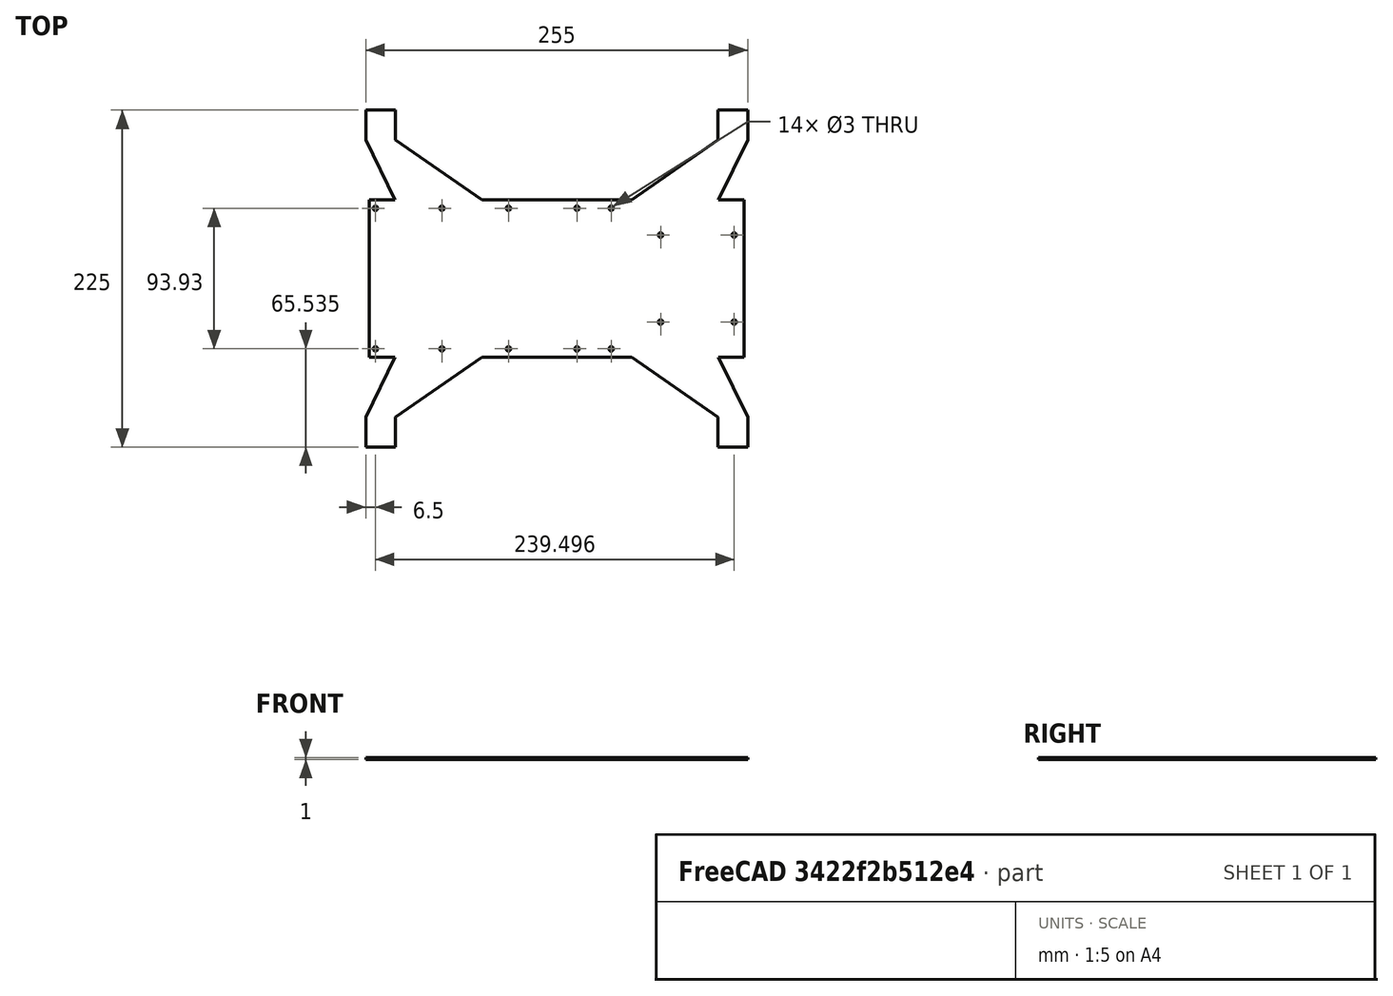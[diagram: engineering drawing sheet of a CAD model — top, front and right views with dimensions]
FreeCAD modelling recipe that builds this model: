
FCSTD DOCUMENT  (FreeCAD 0.20R25742 (Git))
Label: Electronics_Standoff
License: All rights reserved
LicenseURL: http://en.wikipedia.org/wiki/All_rights_reserved
objects: TechDraw::DrawViewDimension×2, Sketcher::SketchObject×1, PartDesign::Pad×1, PartDesign::Body×1, TechDraw::DrawSVGTemplate×1, TechDraw::DrawProjGroupItem×1, TechDraw::DrawProjGroup×1, TechDraw::DrawPage×1
note: 4 computed .brp shape members not serialized (recipe doc carries the construction recipe); baked Part::Feature solids carry a one-line shape summary decoded from their .brp

FEATURE [Sketcher::SketchObject] Sketch
  FullyConstrained = true
  MapMode = 5
  Support = -> [XY_Plane]
  sketch-geometry (42):
    g0: LineSegment StartX=-125 StartY=52.5 StartZ=0 EndX=-108 EndY=52.5 EndZ=0
    g1: LineSegment StartX=125 StartY=52.5 StartZ=0 EndX=125 EndY=-52.5 EndZ=0
    g2: LineSegment StartX=125 StartY=-52.5 StartZ=0 EndX=108 EndY=-52.5 EndZ=0
    g3: LineSegment StartX=-125 StartY=-52.5 StartZ=0 EndX=-125 EndY=52.5 EndZ=0
    g4: Circle CenterX=-121 CenterY=-46.965 CenterZ=0 NormalX=0 NormalY=0 NormalZ=1 AngleXU=0 Radius=1.5
    g5: Circle CenterX=-76.58 CenterY=-46.965 CenterZ=0 NormalX=0 NormalY=0 NormalZ=1 AngleXU=0 Radius=1.5
    g6: Circle CenterX=-32.16 CenterY=-46.965 CenterZ=0 NormalX=0 NormalY=0 NormalZ=1 AngleXU=0 Radius=1.5
    g7: Circle CenterX=13.54 CenterY=-46.965 CenterZ=0 NormalX=0 NormalY=0 NormalZ=1 AngleXU=0 Radius=1.5
    g8: Circle CenterX=36.41 CenterY=-46.965 CenterZ=0 NormalX=0 NormalY=0 NormalZ=1 AngleXU=0 Radius=1.5
    g9: Circle CenterX=36.41 CenterY=46.965 CenterZ=0 NormalX=0 NormalY=0 NormalZ=1 AngleXU=0 Radius=1.5
    g10: Circle CenterX=13.54 CenterY=46.965 CenterZ=0 NormalX=0 NormalY=0 NormalZ=1 AngleXU=0 Radius=1.5
    g11: Circle CenterX=-32.16 CenterY=46.965 CenterZ=0 NormalX=0 NormalY=0 NormalZ=1 AngleXU=0 Radius=1.5
    g12: Circle CenterX=-76.58 CenterY=46.965 CenterZ=0 NormalX=0 NormalY=0 NormalZ=1 AngleXU=0 Radius=1.5
    g13: Circle CenterX=-121 CenterY=46.965 CenterZ=0 NormalX=0 NormalY=0 NormalZ=1 AngleXU=0 Radius=1.5
    g14: Circle CenterX=69.3563 CenterY=29.07 CenterZ=0 NormalX=0 NormalY=0 NormalZ=1 AngleXU=0 Radius=1.5
    g15: Circle CenterX=118.496 CenterY=29.07 CenterZ=0 NormalX=0 NormalY=0 NormalZ=1 AngleXU=0 Radius=1.5
    g16: Circle CenterX=69.3563 CenterY=-29.07 CenterZ=0 NormalX=0 NormalY=0 NormalZ=1 AngleXU=0 Radius=1.5
    g17: Circle CenterX=118.496 CenterY=-29.07 CenterZ=0 NormalX=0 NormalY=0 NormalZ=1 AngleXU=0 Radius=1.5
    g18: LineSegment StartX=108 StartY=52.5 StartZ=0 EndX=127.5 EndY=92.5 EndZ=0
    g19: LineSegment StartX=127.5 StartY=92.5 StartZ=0 EndX=127.5 EndY=112.5 EndZ=0
    g20: LineSegment StartX=127.5 StartY=112.5 StartZ=0 EndX=107.5 EndY=112.5 EndZ=0
    g21: LineSegment StartX=107.5 StartY=112.5 StartZ=0 EndX=107.5 EndY=92.5 EndZ=0
    g22: LineSegment StartX=107.5 StartY=92.5 StartZ=0 EndX=50 EndY=52.5 EndZ=0
    g23: LineSegment StartX=-108 StartY=52.5 StartZ=0 EndX=-127.5 EndY=92.5 EndZ=0
    g24: LineSegment StartX=-127.5 StartY=92.5 StartZ=0 EndX=-127.5 EndY=112.5 EndZ=0
    g25: LineSegment StartX=-127.5 StartY=112.5 StartZ=0 EndX=-107.5 EndY=112.5 EndZ=0
    g26: LineSegment StartX=-107.5 StartY=112.5 StartZ=0 EndX=-107.5 EndY=92.5 EndZ=0
    g27: LineSegment StartX=-107.5 StartY=92.5 StartZ=0 EndX=-50 EndY=52.5 EndZ=0
    g28: LineSegment StartX=-108 StartY=-52.5 StartZ=0 EndX=-127.5 EndY=-92.5 EndZ=0
    g29: LineSegment StartX=-127.5 StartY=-92.5 StartZ=0 EndX=-127.5 EndY=-112.5 EndZ=0
    g30: LineSegment StartX=-127.5 StartY=-112.5 StartZ=0 EndX=-107.5 EndY=-112.5 EndZ=0
    g31: LineSegment StartX=-107.5 StartY=-112.5 StartZ=0 EndX=-107.5 EndY=-92.5 EndZ=0
    g32: LineSegment StartX=-107.5 StartY=-92.5 StartZ=0 EndX=-50 EndY=-52.5 EndZ=0
    g33: LineSegment StartX=108 StartY=-52.5 StartZ=0 EndX=127.5 EndY=-92.5 EndZ=0
    g34: LineSegment StartX=127.5 StartY=-92.5 StartZ=0 EndX=127.5 EndY=-112.5 EndZ=0
    g35: LineSegment StartX=127.5 StartY=-112.5 StartZ=0 EndX=107.5 EndY=-112.5 EndZ=0
    g36: LineSegment StartX=107.5 StartY=-112.5 StartZ=0 EndX=107.5 EndY=-92.5 EndZ=0
    g37: LineSegment StartX=107.5 StartY=-92.5 StartZ=0 EndX=50 EndY=-52.5 EndZ=0
    g38: LineSegment StartX=-50 StartY=52.5 StartZ=0 EndX=50 EndY=52.5 EndZ=0
    g39: LineSegment StartX=108 StartY=52.5 StartZ=0 EndX=125 EndY=52.5 EndZ=0
    g40: LineSegment StartX=50 StartY=-52.5 StartZ=0 EndX=-50 EndY=-52.5 EndZ=0
    g41: LineSegment StartX=-108 StartY=-52.5 StartZ=0 EndX=-125 EndY=-52.5 EndZ=0
  constraints (121):
    c: Coincident(g39,g1)
    c: Coincident(g1,g2)
    c: Coincident(g41,g3)
    c: Coincident(g3,g0)
    c: Horizontal(g0)
    c: Horizontal(g2)
    c: Vertical(g1)
    c: Vertical(g3)
    c: Symmetric(g1,g0,g-1)
    c: DistanceY(g3,g3) = 105
    c: DistanceX(g0,g39) = 250
    c: Diameter(g4) = 3
    c: Horizontal(g7,g6)
    c: Horizontal(g6,g5)
    c: Horizontal(g5,g4)
    c: Horizontal(g4,g8)
    c: Horizontal(g13,g12)
    c: Horizontal(g12,g11)
    c: Horizontal(g11,g10)
    c: Horizontal(g10,g9)
    c: Equal(g4,g5)
    c: Equal(g5,g6)
    c: Equal(g6,g7)
    c: Equal(g7,g8)
    c: Equal(g8,g9)
    c: Equal(g9,g10)
    c: Equal(g10,g11)
    c: Equal(g11,g12)
    c: Equal(g12,g13)
    c: Symmetric(g13,g4,g-1)
    c: DistanceY(g4,g13) = 93.93
    c: Vertical(g5,g12)
    c: DistanceX(g13,g12) = 44.42
    c: Vertical(g11,g6)
    c: Vertical(g10,g7)
    c: Vertical(g9,g8)
    c: DistanceX(g12,g11) = 44.42
    c: DistanceX(g11,g10) = 45.7
    c: DistanceX(g10,g9) = 22.87
    c: Horizontal(g14,g15)
    c: Horizontal(g16,g17)
    c: Vertical(g17,g15)
    c: Equal(g14,g15)
    c: Equal(g15,g17)
    c: Equal(g17,g16)
    c: Equal(g16,g13)
    c: Symmetric(g14,g16,g-1)
    c: DistanceY(g16,g14) = 58.14
    c: DistanceX(g14,g15) = 49.14
    c: Block(g14)
    c: DistanceX(g0,g13) = 4
    c: PointOnObject(g18,g0)
    c: Coincident(g18,g19)
    c: Vertical(g19)
    c: Coincident(g19,g20)
    c: Horizontal(g20)
    c: Coincident(g20,g21)
    c: Vertical(g21)
    c: Coincident(g21,g22)
    c: PointOnObject(g22,g0)
    c: Coincident(g23,g24)
    c: Coincident(g24,g25)
    c: Horizontal(g25)
    c: Coincident(g25,g26)
    c: Coincident(g26,g27)
    c: PointOnObject(g28,g2)
    c: Coincident(g28,g29)
    c: Vertical(g29)
    c: Coincident(g29,g30)
    c: Coincident(g30,g31)
    c: Coincident(g31,g32)
    c: PointOnObject(g32,g2)
    c: Coincident(g33,g34)
    c: Vertical(g34)
    c: Coincident(g34,g35)
    c: Coincident(g35,g36)
    c: Coincident(g36,g37)
    c: DistanceY(g22,g21) = 40
    c: Horizontal(g21,g18)
    c: Horizontal(g26,g23)
    c: DistanceY(g36,g37) = 40
    c: Horizontal(g33,g36)
    c: Horizontal(g31,g28)
    c: Horizontal(g30)
    c: Horizontal(g35)
    c: Vertical(g26)
    c: Vertical(g24)
    c: Vertical(g31)
    c: Vertical(g36)
    c: Symmetric(g36,g31,g-2)
    c: Symmetric(g26,g21,g-2)
    c: DistanceX(g25,g25) = 20
    c: Equal(g20,g25)
    c: Equal(g25,g30)
    c: Equal(g30,g35)
    c: Symmetric(g27,g22,g-2)
    c: Vertical(g22,g37)
    c: Vertical(g33,g18)
    c: Vertical(g32,g27)
    c: Vertical(g23,g28)
    c: Vertical(g21,g36)
    c: Coincident(g0,g23)
    c: PointOnObject(g38,g27)
    c: Coincident(g2,g33)
    c: Coincident(g40,g37)
    c: DistanceX(g0,g27) = 58
    c: DistanceX(g22,g18) = 58
    c: Coincident(g18,g39)
    c: Horizontal(g39)
    c: Coincident(g22,g38)
    c: Horizontal(g38)
    c: Horizontal(g41)
    c: Coincident(g28,g41)
    c: Coincident(g32,g40)
    c: Horizontal(g40)
    c: DistanceX(g32,g37) = 100
    c: Horizontal(g25,g20)
    c: Horizontal(g30,g35)
    c: DistanceX(g26,g21) = 215
    c: DistanceY(g24,g24) = 20
    c: Equal(g29,g24)
FEATURE [PartDesign::Pad] Pad
  Direction = (0,0,1)
  Length = 1
  Length2 = 100
  Profile = -> Sketch
  Type = 0
FEATURE [PartDesign::Body] Body
  Group = -> [Sketch,Pad]
  Origin = -> Origin
  Tip = -> Pad
FEATURE [TechDraw::DrawSVGTemplate] Template
  EditableTexts = Designed_by_Name=Designed by Name; Drawing_number=Drawing number; FC-Date=Date; FC-SC=Scale; FC-SH=Sheet; FC-Title=Title; Subtitle=Subtitle; Weight=Weight
  Height = 210
  Orientation = 1
  Width = 297
FEATURE [TechDraw::DrawProjGroupItem] ProjItem  label="Front"
  CoarseView = false
  Direction = (0,0,1)
  Focus = 100
  HardHidden = false
  IsoCount = 0
  IsoHidden = false
  IsoVisible = false
  LockPosition = true
  Perspective = false
  Rotation = 0
  RotationVector = (1,0,0)
  ScaleType = 2
  SeamHidden = false
  SeamVisible = true
  SmoothHidden = false
  SmoothVisible = true
  Source = -> [Pad]
  Type = 0
  X = 0
  XDirection = (1,0,0)
  Y = 0
FEATURE [TechDraw::DrawProjGroup] ProjGroup
  Anchor = -> ProjItem
  AutoDistribute = true
  LockPosition = false
  ProjectionType = 0
  Rotation = 0
  ScaleType = 0
  Source = -> [Pad]
  Views = -> [ProjItem]
  X = 148.5
  Y = 105
  spacingX = 15
  spacingY = 15
FEATURE [TechDraw::DrawViewDimension] Dimension
  Arbitrary = false
  ArbitraryTolerances = false
  EqualTolerance = true
  FormatSpec = %.2f
  FormatSpecOverTolerance = %+.2f
  FormatSpecUnderTolerance = %+.2f
  Inverted = false
  LockPosition = false
  MeasureType = 1
  OverTolerance = 0
  References2D = -> [ProjItem]
  Rotation = 0
  ScaleType = 0
  TheoreticalExact = false
  Type = 1
  UnderTolerance = 0
  X = -16.3147
  Y = 71.743
FEATURE [TechDraw::DrawViewDimension] Dimension001
  Arbitrary = false
  ArbitraryTolerances = false
  EqualTolerance = true
  FormatSpec = %.2f
  FormatSpecOverTolerance = %+.2f
  FormatSpecUnderTolerance = %+.2f
  Inverted = false
  LockPosition = false
  MeasureType = 1
  OverTolerance = 0
  References2D = -> [ProjItem]
  Rotation = 0
  ScaleType = 0
  TheoreticalExact = false
  Type = 1
  UnderTolerance = 0
  X = -12.5498
  Y = 86.2251
FEATURE [TechDraw::DrawPage] Page
  KeepUpdated = true
  NextBalloonIndex = 1
  ProjectionType = 0
  Template = -> Template
  Views = -> [ProjGroup,Dimension,Dimension001]
